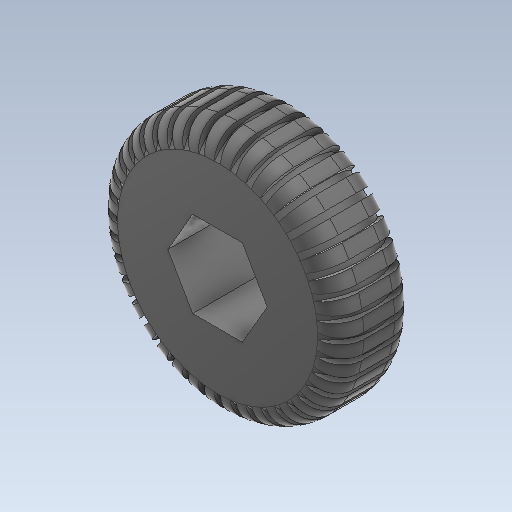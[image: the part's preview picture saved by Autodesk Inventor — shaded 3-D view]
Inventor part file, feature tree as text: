
AUTODESK INVENTOR PART (.ipt)
format: ipt  version: 2020.4 (Build 244396000, 396)  size: 701,952 bytes
history: native  units: mm
features: extrude x2, sketch x2, fillet x1, pattern_circular x1
ambient origin geometry x8: Origin, YZ Plane, XZ Plane, XY Plane, X Axis, Y Axis, Z Axis, Center Point
bodies: Solid1 (feature_tree)
feature tree (6):
  extrude  "Extrusion1"  Depth=16.0mm
  fillet  "Fillet1"  Radius=5.0mm
  extrude  "Extrusion2"  Depth=0.4mm
  pattern_circular  "Circular Pattern1"  [2 undecoded]
  sketch  "Sketch1"  dims[d1=5.6mm d2=16.0mm d3=5.0mm d4=0.0mm]
  sketch  "Sketch2"  dims[d5=90.0deg d6=6.5mm d7=3.25mm d8=0.4mm d9=0.0mm d10=400.0mm d11=360.0deg d13=1.5mm]
note: 2 required parameter values undecoded (feature->parameter linkage not recoverable at this tier; creation-order binding heuristic only, values carry confidence <= 0.55)
